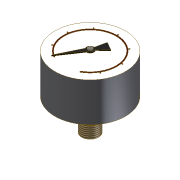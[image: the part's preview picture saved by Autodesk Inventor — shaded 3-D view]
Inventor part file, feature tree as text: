
AUTODESK INVENTOR PART (.ipt)
format: ipt  version: 2014 (Build 180170000, 170)  size: 160,768 bytes
history: native  units: mm
features: imported_body x1, thread x1
ambient origin geometry x8: Origin, YZ Plane, XZ Plane, XY Plane, X Axis, Y Axis, Z Axis, Center Point
bodies: Solid1 (feature_tree)
feature tree (2):
  imported_body  "Base1"
  thread  "Thread1"  [1 undecoded]
note: 1 required parameter value undecoded (feature->parameter linkage not recoverable at this tier; creation-order binding heuristic only, values carry confidence <= 0.55)
